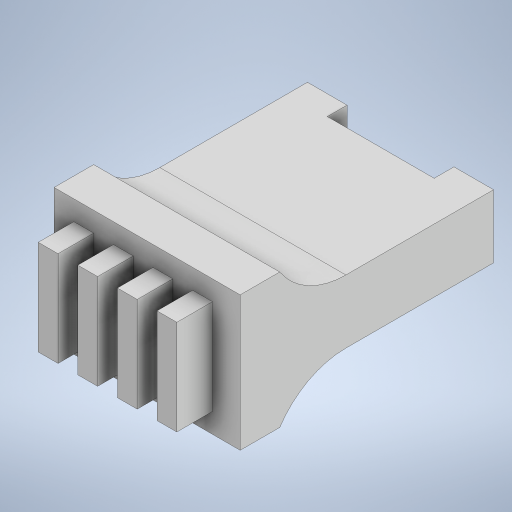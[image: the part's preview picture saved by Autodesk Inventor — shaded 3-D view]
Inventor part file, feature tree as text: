
AUTODESK INVENTOR PART (.ipt)
format: ipt  version: 2023 (Build 270158000, 158)  size: 326,656 bytes
history: native  units: in
note: dims shown in document units (in); Inventor stores cm internally (conversion verified against a paired STEP export)
features: reference x18, other x7, extrude x6, sketch x6, projected_geometry x6, fillet x1
ambient origin geometry x8: Origin, YZ Plane, XZ Plane, XY Plane, X Axis, Y Axis, Z Axis, Center Point
bodies: Body1 (feature_tree)
feature tree (44):
  other  "Bryła1"
  extrude  "Wyciągnięcie proste1"  Depth=0.0079in
  sketch  "Szkic2"
  other  "Płaszczyzna konstrukcyjna1"
  extrude  "Wyciągnięcie proste2"  Depth=0.0394in
  extrude  "Wyciągnięcie proste3"  Depth=0.0394in
  extrude  "Wyciągnięcie proste4"  Depth=0.0197in TaperAngle=0.0deg
  extrude  "Wyciągnięcie proste5"  Depth=0.0197in TaperAngle=0.0deg
  extrude  "Wyciągnięcie proste6"  Depth=0.0039in
  fillet  "Zaokrąglenie1"  Radius=0.0394in
  sketch  "Szkic1"
  reference  "Odniesienie1"
  reference  "Odniesienie2"
  reference  "Odniesienie3"
  reference  "Odniesienie4"
  reference  "Odniesienie5"
  reference  "Odniesienie6"
  reference  "Odniesienie7"
  reference  "Odniesienie8"
  reference  "Odniesienie9"
  reference  "Odniesienie10"
  projected_geometry  "Pętla rzutowana1"
  projected_geometry  "Pętla rzutowana2"
  sketch  "Szkic3"
  reference  "Odniesienie11"
  reference  "Odniesienie12"
  reference  "Odniesienie13"
  reference  "Odniesienie14"
  projected_geometry  "Pętla rzutowana3"
  sketch  "Szkic4"
  reference  "Odniesienie15"
  reference  "Odniesienie16"
  reference  "Odniesienie17"
  reference  "Odniesienie18"
  projected_geometry  "Pętla rzutowana4"
  sketch  "Szkic5"
  projected_geometry  "Pętla rzutowana5"
  sketch  "Szkic6"
  projected_geometry  "Pętla rzutowana6"
  other  "<userpath>\Desktop\MojeRoboty\Stefan\mechanics 2\STEFAN.iam"
  other  "STEFAN.iam"
  other  "plytka_dol:1"
  other  "wlacznik:1"
  other  "SCIANA_LEWA_NOWA_2:1"
